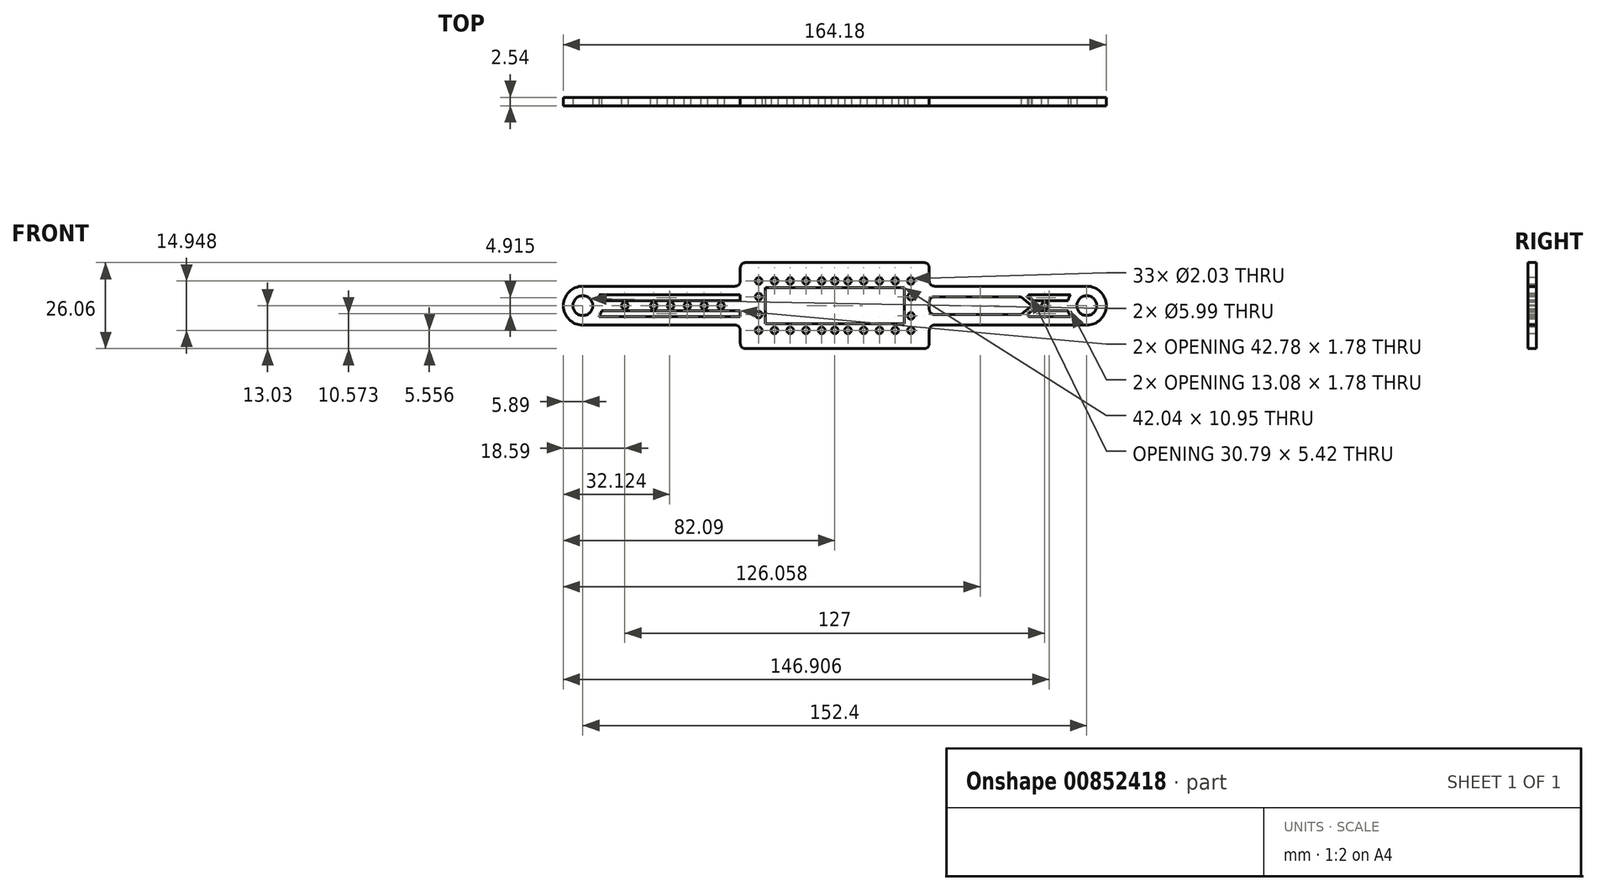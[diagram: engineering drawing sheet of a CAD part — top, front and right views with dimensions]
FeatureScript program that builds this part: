
annotation { "Feature Type Name" : "Feature", "Feature Type Description" : "" }
export const myFeature = defineFeature(function(context is Context, id is Id, definition is map)
    precondition{}
    {
        {
            var Q0;
            Q0=qCreatedBy(makeId("Front.planeOp"),FACE);
            var sketch = newSketch(context, id + "F0", { "sketchPlane" : qUnion([Q0])});
            skLineSegment(sketch, "E0.bottom", {"start": v(-76.2, -5.89) * mm, "end": v(-28.57, -5.89) * mm});
            skLineSegment(sketch, "E0.top", {"start": v(-76.2, 5.89) * mm, "end": v(-28.58, 5.89) * mm});
            skCircle(sketch, "E1", {"center": v(-76.2, 0) * mm, "radius": 3 * mm});
            skCircle(sketch, "E2", {"center": v(76.2, 0) * mm, "radius": 3 * mm});
            skLineSegment(sketch, "E3.bottom", {"start": v(-28.58, 13.03) * mm, "end": v(28.58, 13.03) * mm});
            skLineSegment(sketch, "E3.top", {"start": v(-28.58, -13.03) * mm, "end": v(28.58, -13.03) * mm});
            skLineSegment(sketch, "E3.left", {"start": v(-28.58, 13.03) * mm, "end": v(-28.58, 5.89) * mm});
            skLineSegment(sketch, "E3.right", {"start": v(28.58, 13.03) * mm, "end": v(28.58, 5.89) * mm});
            skArc(sketch, "E4", {"start": v(76.2, -5.89) * mm, "mid": v(82.09, 0) * mm, "end": v(76.2, 5.89) * mm});
            skArc(sketch, "E5", {"start": v(-76.2, 5.89) * mm, "mid": v(-82.09, 0) * mm, "end": v(-76.2, -5.89) * mm});
            skLineSegment(sketch, "E6.trimOffspring", {"start": v(-28.58, -5.89) * mm, "end": v(-28.58, -13.03) * mm});
            skLineSegment(sketch, "E7.trimOffspring", {"start": v(28.58, -5.89) * mm, "end": v(28.58, -13.03) * mm});
            skLineSegment(sketch, "E8.trimOffspring", {"start": v(28.58, 5.89) * mm, "end": v(76.2, 5.89) * mm});
            skLineSegment(sketch, "E9.trimOffspring", {"start": v(28.58, -5.89) * mm, "end": v(76.2, -5.89) * mm});
            skLineSegment(sketch, "E10.right", {"start": v(-34.42, 2.71) * mm, "end": v(-34.42, -2.71) * mm});
            skLineSegment(sketch, "E11.bottom", {"start": v(28.58, 2.71) * mm, "end": v(56.28, 2.71) * mm});
            skLineSegment(sketch, "E11.top", {"start": v(28.58, -2.71) * mm, "end": v(56.28, -2.71) * mm});
            skLineSegment(sketch, "E11.left", {"start": v(28.58, 2.71) * mm, "end": v(28.58, -2.71) * mm});
            skPoint(sketch, "E12", {"position": v(-23.02, 7.47) * mm});
            skPoint(sketch, "E13", {"position": v(-18.26, 7.47) * mm});
            skPoint(sketch, "E14", {"position": v(-13.5, 7.47) * mm});
            skPoint(sketch, "E15", {"position": v(-8.73, 7.47) * mm});
            skPoint(sketch, "E16", {"position": v(-3.97, 7.47) * mm});
            skPoint(sketch, "E17", {"position": v(0, 7.47) * mm});
            skPoint(sketch, "E18", {"position": v(3.97, 7.47) * mm});
            skPoint(sketch, "E19", {"position": v(8.73, 7.47) * mm});
            skPoint(sketch, "E20", {"position": v(13.5, 7.47) * mm});
            skPoint(sketch, "E21", {"position": v(18.26, 7.47) * mm});
            skPoint(sketch, "E22", {"position": v(23.02, 7.47) * mm});
            skPoint(sketch, "E23", {"position": v(23.02, 2.71) * mm});
            skPoint(sketch, "E24", {"position": v(23.02, -2.71) * mm});
            skPoint(sketch, "E25", {"position": v(23.02, -7.47) * mm});
            skPoint(sketch, "E26", {"position": v(18.26, -7.47) * mm});
            skPoint(sketch, "E27", {"position": v(13.5, -7.47) * mm});
            skPoint(sketch, "E28", {"position": v(8.73, -7.47) * mm});
            skPoint(sketch, "E29", {"position": v(3.97, -7.47) * mm});
            skPoint(sketch, "E30", {"position": v(0, -7.47) * mm});
            skPoint(sketch, "E31", {"position": v(-3.97, -7.47) * mm});
            skPoint(sketch, "E32", {"position": v(-8.73, -7.47) * mm});
            skPoint(sketch, "E33", {"position": v(-13.5, -7.47) * mm});
            skPoint(sketch, "E34", {"position": v(-18.26, -7.47) * mm});
            skPoint(sketch, "E35", {"position": v(-23.02, -7.47) * mm});
            skPoint(sketch, "E36", {"position": v(-23.02, -2.71) * mm});
            skPoint(sketch, "E37", {"position": v(-23.02, 2.71) * mm});
            skCircle(sketch, "E38", {"center": v(63.5, 0) * mm, "radius": 1.02 * mm});
            skCircle(sketch, "E39", {"center": v(-63.5, 0) * mm, "radius": 1.02 * mm});
            skLineSegment(sketch, "E40", {"start": v(-33.4, 0) * mm, "end": v(-55.75, 0) * mm});
            skPoint(sketch, "E41", {"position": v(-54.74, 0) * mm});
            skCircle(sketch, "E42", {"center": v(-54.74, 0) * mm, "radius": 1.02 * mm});
            skCircle(sketch, "E43", {"center": v(-49.66, 0) * mm, "radius": 1.02 * mm});
            skCircle(sketch, "E44", {"center": v(-44.58, 0) * mm, "radius": 1.02 * mm});
            skCircle(sketch, "E45", {"center": v(-39.5, 0) * mm, "radius": 1.02 * mm});
            skCircle(sketch, "E46", {"center": v(-34.42, 0) * mm, "radius": 1.02 * mm});
            skLineSegment(sketch, "E47", {"start": v(-25.4, 10.2) * mm, "end": v(-25.4, -10.36) * mm});
            skLineSegment(sketch, "E48.bottom", {"start": v(-21.02, 5.47) * mm, "end": v(21.02, 5.47) * mm});
            skLineSegment(sketch, "E48.top", {"start": v(-21.02, -5.47) * mm, "end": v(21.02, -5.47) * mm});
            skLineSegment(sketch, "E48.left", {"start": v(-21.02, 5.47) * mm, "end": v(-21.02, -5.47) * mm});
            skLineSegment(sketch, "E48.right", {"start": v(21.02, 5.47) * mm, "end": v(21.02, -5.47) * mm});
            skLineSegment(sketch, "E49.bottom", {"start": v(-71.36, 3.35) * mm, "end": v(-28.58, 3.35) * mm});
            skLineSegment(sketch, "E49.top", {"start": v(-70.53, 1.57) * mm, "end": v(-28.58, 1.57) * mm});
            skLineSegment(sketch, "E49.right", {"start": v(-28.58, 3.35) * mm, "end": v(-28.58, 1.57) * mm});
            skLineSegment(sketch, "E50.bottom", {"start": v(-28.58, -3.35) * mm, "end": v(-71.36, -3.35) * mm});
            skLineSegment(sketch, "E50.top", {"start": v(-28.58, -1.57) * mm, "end": v(-70.53, -1.57) * mm});
            skLineSegment(sketch, "E50.left", {"start": v(-28.57, -3.35) * mm, "end": v(-28.57, -1.57) * mm});
            skPoint(sketch, "E49.left.end.orphan", {"position": v(-69.27, 1.57) * mm});
            skPoint(sketch, "E50.right.end.orphan", {"position": v(-69.27, -1.57) * mm});
            skArc(sketch, "E51.trimOffspring", {"start": v(-70.53, 1.57) * mm, "mid": v(-70.87, 2.5) * mm, "end": v(-71.36, 3.35) * mm});
            skArc(sketch, "E52.trimOffspring", {"start": v(-71.36, -3.35) * mm, "mid": v(-70.87, -2.5) * mm, "end": v(-70.53, -1.57) * mm});
            skLineSegment(sketch, "E53.bottom", {"start": v(58.66, 3.35) * mm, "end": v(71.36, 3.35) * mm});
            skLineSegment(sketch, "E53.top", {"start": v(59.66, 1.57) * mm, "end": v(70.53, 1.57) * mm});
            skLineSegment(sketch, "E54.bottom", {"start": v(59.66, -1.57) * mm, "end": v(70.53, -1.57) * mm});
            skLineSegment(sketch, "E54.top", {"start": v(58.66, -3.35) * mm, "end": v(71.36, -3.35) * mm});
            skArc(sketch, "E55", {"start": v(70.53, -1.57) * mm, "mid": v(70.87, -2.5) * mm, "end": v(71.36, -3.35) * mm});
            skArc(sketch, "E56.trimOffspring", {"start": v(71.36, 3.35) * mm, "mid": v(70.87, 2.5) * mm, "end": v(70.53, 1.57) * mm});
            skArc(sketch, "E57", {"start": v(58.66, 3.35) * mm, "mid": v(58.46, 3.03) * mm, "end": v(58.28, 2.71) * mm});
            skArc(sketch, "E58.trimOffspring", {"start": v(58.28, -2.71) * mm, "mid": v(58.46, -3.03) * mm, "end": v(58.66, -3.35) * mm});
            skArc(sketch, "E59", {"start": v(59.36, 0.17) * mm, "mid": v(59.36, 0) * mm, "end": v(59.36, -0.17) * mm});
            skLineSegment(sketch, "E60", {"start": v(58.28, 2.71) * mm, "end": v(59.66, 1.57) * mm});
            skLineSegment(sketch, "E61", {"start": v(59.66, -1.57) * mm, "end": v(58.28, -2.71) * mm});
            skLineSegment(sketch, "E62", {"start": v(59.36, -0.17) * mm, "end": v(56.28, -2.71) * mm});
            skLineSegment(sketch, "E63", {"start": v(59.36, 0.17) * mm, "end": v(56.28, 2.71) * mm});
            skSolve(sketch);
        }
        {
            var Q0;
            Q0=makeQuery(id+"F0.imprint","IMPRINT",FACE,{"disambiguationData":[TD([[makeQuery(id+"F0.imprint","IMPRINT",EDGE,{"derivedFrom":sQuery(id+"F0.wireOp",EDGE,"E0.bottom")}),1.0]])]});
            extrude(context, id + "F1", {"entities" : qUnion([Q0]), "oppositeDirection" : true, "depth" : 2.54 * mm, "offsetDistance" : 25.4 * mm});
        }
        {
            var Q0;
            Q0=makeQuery(id+"F1.opExtrude","CAP_FACE",FACE,{"disambiguationData":[OSD([sQuery(id+"F0.wireOp",EDGE,"E0.bottom"),sQuery(id+"F0.wireOp",EDGE,"E0.top"),sQuery(id+"F0.wireOp",EDGE,"E1"),sQuery(id+"F0.wireOp",EDGE,"E2"),sQuery(id+"F0.wireOp",EDGE,"E3.bottom"),sQuery(id+"F0.wireOp",EDGE,"E3.top"),sQuery(id+"F0.wireOp",EDGE,"E3.left"),sQuery(id+"F0.wireOp",EDGE,"E3.right"),sQuery(id+"F0.wireOp",EDGE,"E6.trimOffspring"),sQuery(id+"F0.wireOp",EDGE,"E7.trimOffspring"),sQuery(id+"F0.wireOp",EDGE,"E8.trimOffspring"),sQuery(id+"F0.wireOp",EDGE,"E9.trimOffspring"),sQuery(id+"F0.wireOp",EDGE,"E10.bottom"),sQuery(id+"F0.wireOp",EDGE,"E10.top"),sQuery(id+"F0.wireOp",EDGE,"E10.right"),sQuery(id+"F0.wireOp",EDGE,"E11.bottom"),sQuery(id+"F0.wireOp",EDGE,"E11.top"),sQuery(id+"F0.wireOp",EDGE,"E11.left"),sQuery(id+"F0.wireOp",EDGE,"E5"),sQuery(id+"F0.wireOp",EDGE,"xXDYwIl3-2WsI-TLsU-YSiK-TS8SPhgtdWB1"),sQuery(id+"F0.wireOp",EDGE,"fc859af6-107b-40eb-a544-af998087aeb3.trimOffspring"),sQuery(id+"F0.wireOp",EDGE,"E4")])],"isStart":true});
            var sketch = newSketch(context, id + "F2", { "sketchPlane" : qUnion([Q0])});
            skLineSegment(sketch, "E64.bottom", {"start": v(-28.58, 13.03) * mm, "end": v(28.58, 13.03) * mm});
            skLineSegment(sketch, "E64.top", {"start": v(-28.58, -13.03) * mm, "end": v(28.58, -13.03) * mm});
            skPoint(sketch, "E65", {"position": v(-23.02, 7.47) * mm});
            skPoint(sketch, "E66", {"position": v(-18.26, 7.47) * mm});
            skPoint(sketch, "E67", {"position": v(-13.5, 7.47) * mm});
            skPoint(sketch, "E68", {"position": v(-8.73, 7.47) * mm});
            skPoint(sketch, "E69", {"position": v(-3.97, 7.47) * mm});
            skPoint(sketch, "E70", {"position": v(0, 7.47) * mm});
            skPoint(sketch, "E71", {"position": v(3.97, 7.47) * mm});
            skPoint(sketch, "E72", {"position": v(8.73, 7.47) * mm});
            skPoint(sketch, "E73", {"position": v(13.5, 7.47) * mm});
            skPoint(sketch, "E74", {"position": v(18.26, 7.47) * mm});
            skPoint(sketch, "E75", {"position": v(23.01, 7.47) * mm});
            skPoint(sketch, "E76", {"position": v(23.02, 2.71) * mm});
            skPoint(sketch, "E77", {"position": v(23.02, -3.11) * mm});
            skPoint(sketch, "E78", {"position": v(23.02, -7.47) * mm});
            skPoint(sketch, "E79", {"position": v(18.26, -7.47) * mm});
            skPoint(sketch, "E80", {"position": v(13.5, -7.47) * mm});
            skPoint(sketch, "E81", {"position": v(8.73, -7.47) * mm});
            skPoint(sketch, "E82", {"position": v(3.97, -7.47) * mm});
            skPoint(sketch, "E83", {"position": v(0, -7.47) * mm});
            skPoint(sketch, "E84", {"position": v(-3.97, -7.47) * mm});
            skPoint(sketch, "E85", {"position": v(-8.73, -7.47) * mm});
            skPoint(sketch, "E86", {"position": v(-13.5, -7.47) * mm});
            skPoint(sketch, "E87", {"position": v(-18.26, -7.47) * mm});
            skPoint(sketch, "E88", {"position": v(-23.02, -7.47) * mm});
            skPoint(sketch, "E89", {"position": v(-23.02, -2.71) * mm});
            skPoint(sketch, "E90", {"position": v(-23.02, 2.71) * mm});
            skSolve(sketch);
        }
        {
            var Q0;
            Q0=sQuery(id+"F2.wireOp",VERTEX,"E65");
            var Q1;
            Q1=sQuery(id+"F2.wireOp",VERTEX,"E66");
            var Q2;
            Q2=sQuery(id+"F2.wireOp",VERTEX,"E67");
            var Q3;
            Q3=sQuery(id+"F2.wireOp",VERTEX,"E68");
            var Q4;
            Q4=sQuery(id+"F2.wireOp",VERTEX,"E69");
            var Q5;
            Q5=sQuery(id+"F2.wireOp",VERTEX,"E70");
            var Q6;
            Q6=sQuery(id+"F2.wireOp",VERTEX,"E71");
            var Q7;
            Q7=sQuery(id+"F2.wireOp",VERTEX,"E72");
            var Q8;
            Q8=sQuery(id+"F2.wireOp",VERTEX,"E73");
            var Q9;
            Q9=sQuery(id+"F2.wireOp",VERTEX,"E74");
            var Q10;
            Q10=sQuery(id+"F2.wireOp",VERTEX,"E75");
            var Q11;
            Q11=sQuery(id+"F2.wireOp",VERTEX,"E77");
            var Q12;
            Q12=sQuery(id+"F2.wireOp",VERTEX,"E78");
            var Q13;
            Q13=sQuery(id+"F2.wireOp",VERTEX,"E76");
            var Q14;
            Q14=sQuery(id+"F2.wireOp",VERTEX,"E79");
            var Q15;
            Q15=sQuery(id+"F2.wireOp",VERTEX,"E80");
            var Q16;
            Q16=sQuery(id+"F2.wireOp",VERTEX,"E81");
            var Q17;
            Q17=sQuery(id+"F2.wireOp",VERTEX,"E82");
            var Q18;
            Q18=sQuery(id+"F2.wireOp",VERTEX,"E83");
            var Q19;
            Q19=sQuery(id+"F2.wireOp",VERTEX,"E84");
            var Q20;
            Q20=sQuery(id+"F2.wireOp",VERTEX,"E85");
            var Q21;
            Q21=sQuery(id+"F2.wireOp",VERTEX,"E86");
            var Q22;
            Q22=sQuery(id+"F2.wireOp",VERTEX,"E87");
            var Q23;
            Q23=sQuery(id+"F2.wireOp",VERTEX,"E88");
            var Q24;
            Q24=sQuery(id+"F2.wireOp",VERTEX,"E89");
            var Q25;
            Q25=sQuery(id+"F2.wireOp",VERTEX,"E90");
            var Q26;
            Q26=makeQuery(id+"F1.opExtrude","SWEPT_BODY",BODY,{"disambiguationData":[OSD([sQuery(id+"F0.wireOp",EDGE,"E0.bottom"),sQuery(id+"F0.wireOp",EDGE,"E0.top"),sQuery(id+"F0.wireOp",EDGE,"E1"),sQuery(id+"F0.wireOp",EDGE,"E2"),sQuery(id+"F0.wireOp",EDGE,"E3.bottom"),sQuery(id+"F0.wireOp",EDGE,"E3.top"),sQuery(id+"F0.wireOp",EDGE,"E3.left"),sQuery(id+"F0.wireOp",EDGE,"E3.right"),sQuery(id+"F0.wireOp",EDGE,"E6.trimOffspring"),sQuery(id+"F0.wireOp",EDGE,"E7.trimOffspring"),sQuery(id+"F0.wireOp",EDGE,"E8.trimOffspring"),sQuery(id+"F0.wireOp",EDGE,"E9.trimOffspring"),sQuery(id+"F0.wireOp",EDGE,"E10.bottom"),sQuery(id+"F0.wireOp",EDGE,"E10.top"),sQuery(id+"F0.wireOp",EDGE,"E10.right"),sQuery(id+"F0.wireOp",EDGE,"E11.bottom"),sQuery(id+"F0.wireOp",EDGE,"E11.top"),sQuery(id+"F0.wireOp",EDGE,"E11.left"),sQuery(id+"F0.wireOp",EDGE,"E5"),sQuery(id+"F0.wireOp",EDGE,"xXDYwIl3-2WsI-TLsU-YSiK-TS8SPhgtdWB1"),sQuery(id+"F0.wireOp",EDGE,"fc859af6-107b-40eb-a544-af998087aeb3.trimOffspring"),sQuery(id+"F0.wireOp",EDGE,"E4")])]});
            hole(context, id + "F3", {"style" : HoleStyle.SIMPLE, "endStyle" : HoleEndStyle.THROUGH, "holeDiameter" : 2.03 * mm, "majorDiameter" : 6.35 * mm, "isTappedThrough" : true, "tappedDepth" : 3.17 * mm, "tapClearance" : 3, "startFromSketch" : true, "locations" : qUnion([Q0, Q1, Q2, Q3, Q4, Q5, Q6, Q7, Q8, Q9, Q10, Q11, Q12, Q13, Q14, Q15, Q16, Q17, Q18, Q19, Q20, Q21, Q22, Q23, Q24, Q25]), "scope" : qUnion([Q26])});
        }
        {
            var Q0;
            Q0=makeQuery(id+"F1.opExtrude","SWEPT_EDGE",EDGE,{"disambiguationData":[OSD([sQuery(id+"F0.wireOp",EDGE,"E10.right"),sQuery(id+"F0.wireOp",EDGE,"ac3ba209-8f6c-4076-be52-f0ffb78035e8.trimOffspring")])]});
            var Q1;
            Q1=makeQuery(id+"F1.opExtrude","SWEPT_EDGE",EDGE,{"disambiguationData":[OSD([sQuery(id+"F0.wireOp",EDGE,"E10.right"),sQuery(id+"F0.wireOp",EDGE,"a7257af1-2d97-42ae-860f-29a2e6fd8560.trimOffspring")])]});
            var Q2;
            Q2=makeQuery(id+"F1.opExtrude","SWEPT_EDGE",EDGE,{"disambiguationData":[OSD([sQuery(id+"F0.wireOp",EDGE,"E3.bottom"),sQuery(id+"F0.wireOp",EDGE,"E3.left")])]});
            var Q3;
            Q3=makeQuery(id+"F1.opExtrude","SWEPT_EDGE",EDGE,{"disambiguationData":[OSD([sQuery(id+"F0.wireOp",EDGE,"E0.top"),sQuery(id+"F0.wireOp",EDGE,"E3.left")])]});
            var Q4;
            Q4=makeQuery(id+"F1.opExtrude","SWEPT_EDGE",EDGE,{"disambiguationData":[OSD([sQuery(id+"F0.wireOp",EDGE,"E3.top"),sQuery(id+"F0.wireOp",EDGE,"E6.trimOffspring")])]});
            var Q5;
            Q5=makeQuery(id+"F1.opExtrude","SWEPT_EDGE",EDGE,{"disambiguationData":[OSD([sQuery(id+"F0.wireOp",EDGE,"E0.bottom"),sQuery(id+"F0.wireOp",EDGE,"E6.trimOffspring")])]});
            var Q6;
            Q6=makeQuery(id+"F1.opExtrude","SWEPT_EDGE",EDGE,{"disambiguationData":[OSD([sQuery(id+"F0.wireOp",EDGE,"E11.bottom"),sQuery(id+"F0.wireOp",EDGE,"E11.left")])]});
            var Q7;
            Q7=makeQuery(id+"F1.opExtrude","SWEPT_EDGE",EDGE,{"disambiguationData":[OSD([sQuery(id+"F0.wireOp",EDGE,"E3.bottom"),sQuery(id+"F0.wireOp",EDGE,"E3.right")])]});
            var Q8;
            Q8=makeQuery(id+"F1.opExtrude","SWEPT_EDGE",EDGE,{"disambiguationData":[OSD([sQuery(id+"F0.wireOp",EDGE,"E7.trimOffspring"),sQuery(id+"F0.wireOp",EDGE,"E9.trimOffspring")])]});
            var Q9;
            Q9=makeQuery(id+"F1.opExtrude","SWEPT_EDGE",EDGE,{"disambiguationData":[OSD([sQuery(id+"F0.wireOp",EDGE,"E3.top"),sQuery(id+"F0.wireOp",EDGE,"E7.trimOffspring")])]});
            var Q10;
            Q10=makeQuery(id+"F1.opExtrude","SWEPT_EDGE",EDGE,{"disambiguationData":[OSD([sQuery(id+"F0.wireOp",EDGE,"E3.right"),sQuery(id+"F0.wireOp",EDGE,"E8.trimOffspring")])]});
            var Q11;
            Q11=makeQuery(id+"F1.opExtrude","SWEPT_EDGE",EDGE,{"disambiguationData":[OSD([sQuery(id+"F0.wireOp",EDGE,"E11.top"),sQuery(id+"F0.wireOp",EDGE,"E11.left")])]});
            fillet(context, id + "F4", {"entities" : qUnion([Q0, Q1, Q2, Q3, Q4, Q5, Q6, Q7, Q8, Q9, Q10, Q11]), "radius" : 1.59 * mm, "tangentPropagation" : true, "allowEdgeOverflow" : false});
        }
    });
